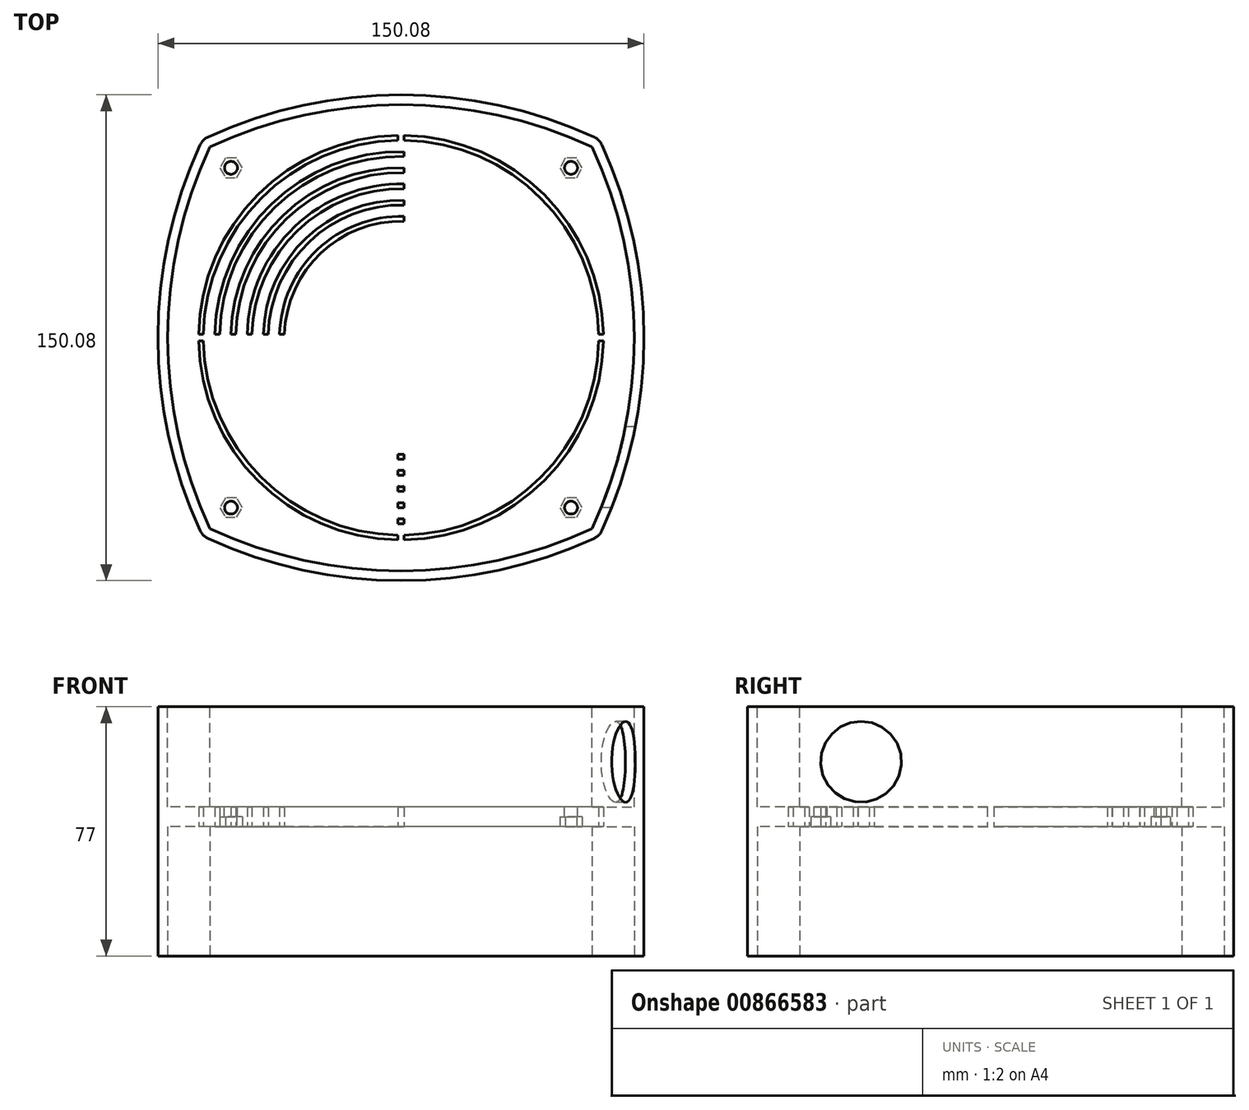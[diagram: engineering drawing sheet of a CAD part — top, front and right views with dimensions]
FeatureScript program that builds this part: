
annotation { "Feature Type Name" : "Feature", "Feature Type Description" : "" }
export const myFeature = defineFeature(function(context is Context, id is Id, definition is map)
    precondition{}
    {
        {
            var Q0;
            Q0=qCreatedBy(makeId("Top.planeOp"),FACE);
            var sketch = newSketch(context, id + "F0", { "sketchPlane" : qUnion([Q0])});
            skLineSegment(sketch, "E0.bottom", {"start": v(196, 49) * mm, "end": v(-196, 49) * mm, "construction": true});
            skLineSegment(sketch, "E0.top", {"start": v(196, -49) * mm, "end": v(-196, -49) * mm, "construction": true});
            skLineSegment(sketch, "E0.left", {"start": v(196, 49) * mm, "end": v(196, -49) * mm, "construction": true});
            skLineSegment(sketch, "E0.right", {"start": v(-196, 49) * mm, "end": v(-196, -49) * mm, "construction": true});
            skPoint(sketch, "E0.middle", {"position": v(0, 0) * mm});
            skLineSegment(sketch, "E1.bottom", {"start": v(207, 59) * mm, "end": v(-207, 59) * mm, "construction": true});
            skLineSegment(sketch, "E1.top", {"start": v(207, -59) * mm, "end": v(-207, -59) * mm, "construction": true});
            skLineSegment(sketch, "E1.left", {"start": v(207, 59) * mm, "end": v(207, -59) * mm, "construction": true});
            skLineSegment(sketch, "E1.right", {"start": v(-207, 59) * mm, "end": v(-207, -59) * mm, "construction": true});
            skLineSegment(sketch, "E2", {"start": v(0, -59) * mm, "end": v(0, 59) * mm, "construction": true});
            skLineSegment(sketch, "E3", {"start": v(-207, 0) * mm, "end": v(207, 0) * mm, "construction": true});
            skCircle(sketch, "E4", {"center": v(0, 0) * mm, "radius": 47.86 * mm});
            skLineSegment(sketch, "E5.bottom", {"start": v(59, 59) * mm, "end": v(-59, 59) * mm, "construction": true});
            skLineSegment(sketch, "E5.top", {"start": v(59, -59) * mm, "end": v(-59, -59) * mm, "construction": true});
            skLineSegment(sketch, "E5.left", {"start": v(59, 59) * mm, "end": v(59, -59) * mm, "construction": true});
            skLineSegment(sketch, "E5.right", {"start": v(-59, 59) * mm, "end": v(-59, -59) * mm, "construction": true});
            skArc(sketch, "E6", {"start": v(59, 59) * mm, "mid": v(0, 72.04) * mm, "end": v(-59, 59) * mm});
            skArc(sketch, "E7", {"start": v(59, -59) * mm, "mid": v(72.04, 0) * mm, "end": v(59, 59) * mm});
            skArc(sketch, "E8", {"start": v(-59, -59) * mm, "mid": v(0, -72.04) * mm, "end": v(59, -59) * mm});
            skArc(sketch, "E9", {"start": v(-59, 59) * mm, "mid": v(-72.04, 0) * mm, "end": v(-59, -59) * mm});
            skArc(sketch, "E10.0", {"start": v(61.26, 61.26) * mm, "mid": v(0, 75.04) * mm, "end": v(-61.26, 61.26) * mm});
            skArc(sketch, "E10.1", {"start": v(61.26, -61.26) * mm, "mid": v(75.04, 0) * mm, "end": v(61.26, 61.26) * mm});
            skArc(sketch, "E10.2", {"start": v(-61.26, -61.26) * mm, "mid": v(0, -75.04) * mm, "end": v(61.26, -61.26) * mm});
            skArc(sketch, "E10.3", {"start": v(-61.26, 61.26) * mm, "mid": v(-75.04, 0) * mm, "end": v(-61.26, -61.26) * mm});
            skSolve(sketch);
        }
        {
            var Q0;
            {var subQ8=sQuery(id+"F0.wireOp",EDGE,"E6");Q0=makeQuery(id+"F0.imprint","IMPRINT",FACE,{"disambiguationData":[TD([[makeQuery(id+"F0.imprint","IMPRINT",EDGE,{"derivedFrom":subQ8}),-1.0]])]});}
            var Q1;
            {var subQ0=sQuery(id+"F0.wireOp",EDGE,"E10.1");var subQ1=sQuery(id+"F0.wireOp",EDGE,"2c3d49d2-39e6-4b7c-b00d-7af9e24e8e71.0");var subQ2=makeQuery(id+"F0.imprint","INTERSECT",VERTEX,{"disambiguationData":[OD(0.0)],"derivedFrom":[subQ1,subQ0]});Q1=makeQuery(id+"F0.imprint","IMPRINT",FACE,{"disambiguationData":[TD([[makeQuery(id+"F0.imprint","IMPRINT",EDGE,{"disambiguationData":[TD([[subQ2,-1.0]])],"derivedFrom":subQ1}),1.0]])]});}
            extrude(context, id + "F1", {"entities" : qUnion([Q0, Q1]), "endBound" : BoundingType.SYMMETRIC, "depth" : 160 * mm, "offsetDistance" : 25 * mm});
        }
        {
            var Q0;
            Q0=qCreatedBy(makeId("Right.planeOp"),FACE);
            var sketch = newSketch(context, id + "F2", { "sketchPlane" : qUnion([Q0])});
            skCircle(sketch, "E11", {"center": v(-294.04, 1407.06) * mm, "radius": 1379.34 * mm});
            skLineSegment(sketch, "E12", {"start": v(0, 0) * mm, "end": v(-237.77, 0) * mm, "construction": true});
            skCircle(sketch, "E13.MirrorC", {"center": v(-294.04, -1407.06) * mm, "radius": 1379.34 * mm});
            skSolve(sketch);
        }
        {
            var Q0;
            Q0=makeQuery(id+"F2.imprint","IMPRINT",FACE,{"disambiguationData":[TD([[makeQuery(id+"F2.imprint","IMPRINT",EDGE,{"derivedFrom":sQuery(id+"F2.wireOp",EDGE,"E11")}),1.0]])]});
            var Q1;
            Q1=makeQuery(id+"F2.imprint","IMPRINT",FACE,{"disambiguationData":[TD([[makeQuery(id+"F2.imprint","IMPRINT",EDGE,{"derivedFrom":sQuery(id+"F2.wireOp",EDGE,"E13.MirrorC")}),-1.0]])]});
            extrude(context, id + "F3", {"entities" : qUnion([Q0, Q1]), "operationType" : NewBodyOperationType.REMOVE, "endBound" : BoundingType.SYMMETRIC, "oppositeDirection" : true, "depth" : 780 * mm, "offsetDistance" : 25 * mm});
        }
        {
            var Q0;
            Q0=qCreatedBy(makeId("Top.planeOp"),FACE);
            cPlane(context, id + "F4", {"entities" : qUnion([Q0]), "cplaneType" : CPlaneType.OFFSET, "offset" : 40 * mm, "width" : 150 * mm, "height" : 150 * mm});
        }
        {
            var Q0;
            Q0=qCreatedBy(id+"F4.planeOp",FACE);
            var sketch = newSketch(context, id + "F5", { "sketchPlane" : qUnion([Q0])});
            skLineSegment(sketch, "E14.bottom", {"start": v(59, 59) * mm, "end": v(-59, 59) * mm, "construction": true});
            skLineSegment(sketch, "E14.top", {"start": v(59, -59) * mm, "end": v(-59, -59) * mm, "construction": true});
            skLineSegment(sketch, "E14.left", {"start": v(59, 59) * mm, "end": v(59, -59) * mm, "construction": true});
            skLineSegment(sketch, "E14.right", {"start": v(-59, 59) * mm, "end": v(-59, -59) * mm, "construction": true});
            skPoint(sketch, "E14.middle", {"position": v(0, 0) * mm});
            skArc(sketch, "E15", {"start": v(59, 59) * mm, "mid": v(0, 72.04) * mm, "end": v(-59, 59) * mm});
            skArc(sketch, "E16", {"start": v(59, -59) * mm, "mid": v(72.04, 0) * mm, "end": v(59, 59) * mm});
            skArc(sketch, "E17", {"start": v(-59, -59) * mm, "mid": v(0, -72.04) * mm, "end": v(59, -59) * mm});
            skArc(sketch, "E18", {"start": v(-59, 59) * mm, "mid": v(-72.04, 0) * mm, "end": v(-59, -59) * mm});
            skSolve(sketch);
        }
        {
            var Q0;
            Q0=qCreatedBy(makeId("Top.planeOp"),FACE);
            var sketch = newSketch(context, id + "F6", { "sketchPlane" : qUnion([Q0])});
            skLineSegment(sketch, "E19.bottom", {"start": v(59, 59) * mm, "end": v(-59, 59) * mm, "construction": true});
            skLineSegment(sketch, "E19.top", {"start": v(59, -59) * mm, "end": v(-59, -59) * mm, "construction": true});
            skLineSegment(sketch, "E19.left", {"start": v(59, 59) * mm, "end": v(59, -59) * mm, "construction": true});
            skLineSegment(sketch, "E19.right", {"start": v(-59, 59) * mm, "end": v(-59, -59) * mm, "construction": true});
            skPoint(sketch, "E19.middle", {"position": v(0, 0) * mm});
            skArc(sketch, "E20", {"start": v(59, 59) * mm, "mid": v(0, 72.04) * mm, "end": v(-59, 59) * mm});
            skArc(sketch, "E21", {"start": v(59, -59) * mm, "mid": v(72.04, 0) * mm, "end": v(59, 59) * mm});
            skArc(sketch, "E22", {"start": v(-59, -59) * mm, "mid": v(0, -72.04) * mm, "end": v(59, -59) * mm});
            skArc(sketch, "E23", {"start": v(-59, 59) * mm, "mid": v(-72.04, 0) * mm, "end": v(-59, -59) * mm});
            skArc(sketch, "E24.0", {"start": v(61.26, 61.26) * mm, "mid": v(0, 75.04) * mm, "end": v(-61.26, 61.26) * mm});
            skArc(sketch, "E24.1", {"start": v(61.26, -61.26) * mm, "mid": v(75.04, 0) * mm, "end": v(61.26, 61.26) * mm});
            skArc(sketch, "E24.2", {"start": v(-61.26, -61.26) * mm, "mid": v(0, -75.04) * mm, "end": v(61.26, -61.26) * mm});
            skArc(sketch, "E24.3", {"start": v(-61.26, 61.26) * mm, "mid": v(-75.04, 0) * mm, "end": v(-61.26, -61.26) * mm});
            skSolve(sketch);
        }
        {
            var Q0;
            Q0=qSketchRegion(id+"F6",true);
            var Q1;
            Q1=makeQuery(id+"F0.imprint","IMPRINT",FACE,{"disambiguationData":[TD([[makeQuery(id+"F0.imprint","IMPRINT",EDGE,{"derivedFrom":sQuery(id+"F0.wireOp",EDGE,"E4")}),-1.0]])]});
            var Q2;
            Q2=makeQuery(id+"F6.imprint","IMPRINT",FACE,{"disambiguationData":[TD([[makeQuery(id+"F6.imprint","IMPRINT",EDGE,{"derivedFrom":sQuery(id+"F6.wireOp",EDGE,"E20")}),1.0]])]});
            extrude(context, id + "F7", {"entities" : qUnion([Q0, Q1, Q2]), "operationType" : NewBodyOperationType.ADD, "endBound" : BoundingType.SYMMETRIC, "depth" : 80 * mm, "offsetDistance" : 25 * mm});
        }
        {
            var Q0;
            Q0=qCreatedBy(makeId("Top.planeOp"),FACE);
            var sketch = newSketch(context, id + "F8", { "sketchPlane" : qUnion([Q0])});
            skCircle(sketch, "E25", {"center": v(0, 0) * mm, "radius": 47.86 * mm});
            skSolve(sketch);
        }
        {
            var Q1;
            Q1=qSketchRegion(id+"F5",true);
            var Q2;
            Q2=qSketchRegion(id+"F8",true);
            loft(context, id + "F9", {"operationType" : NewBodyOperationType.REMOVE, "sheetProfilesArray" : [{ "sheetProfileEntities" : qUnion([Q1]) }, { "sheetProfileEntities" : qUnion([Q2]) }]});
        }
        {
            var Q0;
            Q0=makeQuery(id+"F0.imprint","IMPRINT",FACE,{"disambiguationData":[TD([[makeQuery(id+"F0.imprint","IMPRINT",EDGE,{"derivedFrom":sQuery(id+"F0.wireOp",EDGE,"E4")}),1.0]])]});
            var sketch = newSketch(context, id + "F10", { "sketchPlane" : qUnion([Q0])});
            skCircle(sketch, "E26", {"center": v(0, 0) * mm, "radius": 42.86 * mm});
            skSolve(sketch);
        }
        {
            var Q0;
            Q0=makeQuery(id+"F10.imprint","IMPRINT",FACE,{"disambiguationData":[TD([[makeQuery(id+"F10.imprint","IMPRINT",EDGE,{"derivedFrom":sQuery(id+"F10.wireOp",EDGE,"E26")}),1.0]])]});
            extrude(context, id + "F11", {"entities" : qUnion([Q0]), "operationType" : NewBodyOperationType.REMOVE, "oppositeDirection" : true, "depth" : 3 * mm, "offsetDistance" : 25 * mm});
        }
        {
            var Q0;
            Q0=qCreatedBy(makeId("Top.planeOp"),FACE);
            cPlane(context, id + "F12", {"entities" : qUnion([Q0]), "cplaneType" : CPlaneType.OFFSET, "offset" : 3 * mm, "oppositeDirection" : true, "width" : 150 * mm, "height" : 150 * mm});
        }
        {
            var Q0;
            Q0=qCreatedBy(id+"F12.planeOp",FACE);
            var sketch = newSketch(context, id + "F13", { "sketchPlane" : qUnion([Q0])});
            skLineSegment(sketch, "E27.bottom", {"start": v(59, 59) * mm, "end": v(-59, 59) * mm, "construction": true});
            skLineSegment(sketch, "E27.top", {"start": v(59, -59) * mm, "end": v(-59, -59) * mm, "construction": true});
            skLineSegment(sketch, "E27.left", {"start": v(59, 59) * mm, "end": v(59, -59) * mm, "construction": true});
            skLineSegment(sketch, "E27.right", {"start": v(-59, 59) * mm, "end": v(-59, -59) * mm, "construction": true});
            skPoint(sketch, "E27.middle", {"position": v(0, 0) * mm});
            skArc(sketch, "E28", {"start": v(59, 59) * mm, "mid": v(0, 72.04) * mm, "end": v(-59, 59) * mm});
            skArc(sketch, "E29", {"start": v(59, -59) * mm, "mid": v(72.04, 0) * mm, "end": v(59, 59) * mm});
            skArc(sketch, "E30", {"start": v(-59, -59) * mm, "mid": v(0, -72.04) * mm, "end": v(59, -59) * mm});
            skArc(sketch, "E31", {"start": v(-59, 59) * mm, "mid": v(-72.04, 0) * mm, "end": v(-59, -59) * mm});
            skSolve(sketch);
        }
        {
            var Q0;
            Q0=qSketchRegion(id+"F13",true);
            extrude(context, id + "F14", {"entities" : qUnion([Q0]), "operationType" : NewBodyOperationType.REMOVE, "oppositeDirection" : true, "depth" : 31 * mm, "offsetDistance" : 25 * mm});
        }
        {
            var Q0;
            Q0=makeQuery(id+"F7.boolean.opBoolean","MERGE",FACE,{"derivedFrom":[makeQuery(id+"F7.opExtrude","CAP_FACE",FACE,{"disambiguationData":[OSD([sQuery(id+"F0.wireOp",EDGE,"E4"),sQuery(id+"F0.wireOp",EDGE,"E6"),sQuery(id+"F0.wireOp",EDGE,"E7"),sQuery(id+"F0.wireOp",EDGE,"E8"),sQuery(id+"F0.wireOp",EDGE,"E9")])],"isStart":true}),makeQuery(id+"F7.opExtrude","CAP_FACE",FACE,{"disambiguationData":[OSD([sQuery(id+"F6.wireOp",EDGE,"E24.0"),sQuery(id+"F6.wireOp",EDGE,"E24.1"),sQuery(id+"F6.wireOp",EDGE,"E24.2"),sQuery(id+"F6.wireOp",EDGE,"E24.3")])],"isStart":true})]});
            var sketch = newSketch(context, id + "F15", { "sketchPlane" : qUnion([Q0])});
            skCircle(sketch, "E32", {"center": v(0, 0) * mm, "radius": 62.5 * mm});
            skCircle(sketch, "E33", {"center": v(0, 0) * mm, "radius": 61 * mm});
            skCircle(sketch, "E34", {"center": v(0, 0) * mm, "radius": 57.5 * mm});
            skCircle(sketch, "E35", {"center": v(0, 0) * mm, "radius": 56 * mm});
            skCircle(sketch, "E36", {"center": v(0, 0) * mm, "radius": 52.5 * mm});
            skCircle(sketch, "E37", {"center": v(0, 0) * mm, "radius": 51 * mm});
            skCircle(sketch, "E38", {"center": v(0, 0) * mm, "radius": 47.5 * mm});
            skCircle(sketch, "E39", {"center": v(0, 0) * mm, "radius": 46 * mm});
            skCircle(sketch, "E40", {"center": v(0, 0) * mm, "radius": 42.5 * mm});
            skCircle(sketch, "E41", {"center": v(0, 0) * mm, "radius": 41 * mm});
            skCircle(sketch, "E42", {"center": v(0, 0) * mm, "radius": 37.5 * mm});
            skCircle(sketch, "E43", {"center": v(0, 0) * mm, "radius": 36 * mm});
            skLineSegment(sketch, "E44.bottom", {"start": v(1, -67) * mm, "end": v(-1, -67) * mm});
            skLineSegment(sketch, "E44.top", {"start": v(1, 67) * mm, "end": v(-1, 67) * mm});
            skLineSegment(sketch, "E44.left", {"start": v(1, -67) * mm, "end": v(1, 67) * mm});
            skLineSegment(sketch, "E44.right", {"start": v(-1, -67) * mm, "end": v(-1, 67) * mm});
            skLineSegment(sketch, "E45.bottom", {"start": v(67.5, -1) * mm, "end": v(-67.5, -1) * mm});
            skLineSegment(sketch, "E45.top", {"start": v(67.5, 1) * mm, "end": v(-67.5, 1) * mm});
            skLineSegment(sketch, "E45.left", {"start": v(67.5, -1) * mm, "end": v(67.5, 1) * mm});
            skLineSegment(sketch, "E45.right", {"start": v(-67.5, -1) * mm, "end": v(-67.5, 1) * mm});
            skSolve(sketch);
        }
        {
            var Q0;
            {var subQ0=sQuery(id+"F15.wireOp",EDGE,"E44.right");var subQ1=sQuery(id+"F15.wireOp",EDGE,"E32");var subQ2=makeQuery(id+"F15.imprint","INTERSECT",VERTEX,{"disambiguationData":[OD(0.0)],"derivedFrom":[subQ1,subQ0]});Q0=makeQuery(id+"F15.imprint","IMPRINT",FACE,{"disambiguationData":[TD([[makeQuery(id+"F15.imprint","IMPRINT",EDGE,{"disambiguationData":[TD([[subQ2,-1.0]])],"derivedFrom":subQ1}),1.0]])]});}
            var Q1;
            {var subQ0=sQuery(id+"F15.wireOp",EDGE,"E44.right");var subQ1=sQuery(id+"F15.wireOp",EDGE,"E34");var subQ2=makeQuery(id+"F15.imprint","INTERSECT",VERTEX,{"disambiguationData":[OD(0.0)],"derivedFrom":[subQ1,subQ0]});Q1=makeQuery(id+"F15.imprint","IMPRINT",FACE,{"disambiguationData":[TD([[makeQuery(id+"F15.imprint","IMPRINT",EDGE,{"disambiguationData":[TD([[subQ2,-1.0]])],"derivedFrom":subQ1}),1.0]])]});}
            var Q2;
            {var subQ0=sQuery(id+"F15.wireOp",EDGE,"E44.right");var subQ1=sQuery(id+"F15.wireOp",EDGE,"E36");var subQ2=makeQuery(id+"F15.imprint","INTERSECT",VERTEX,{"disambiguationData":[OD(0.0)],"derivedFrom":[subQ1,subQ0]});Q2=makeQuery(id+"F15.imprint","IMPRINT",FACE,{"disambiguationData":[TD([[makeQuery(id+"F15.imprint","IMPRINT",EDGE,{"disambiguationData":[TD([[subQ2,-1.0]])],"derivedFrom":subQ1}),1.0]])]});}
            var Q3;
            {var subQ0=sQuery(id+"F15.wireOp",EDGE,"E44.right");var subQ1=sQuery(id+"F15.wireOp",EDGE,"E38");var subQ2=makeQuery(id+"F15.imprint","INTERSECT",VERTEX,{"disambiguationData":[OD(0.0)],"derivedFrom":[subQ1,subQ0]});Q3=makeQuery(id+"F15.imprint","IMPRINT",FACE,{"disambiguationData":[TD([[makeQuery(id+"F15.imprint","IMPRINT",EDGE,{"disambiguationData":[TD([[subQ2,-1.0]])],"derivedFrom":subQ1}),1.0]])]});}
            var Q4;
            {var subQ0=sQuery(id+"F15.wireOp",EDGE,"E44.right");var subQ1=sQuery(id+"F15.wireOp",EDGE,"E40");var subQ2=makeQuery(id+"F15.imprint","INTERSECT",VERTEX,{"disambiguationData":[OD(0.0)],"derivedFrom":[subQ1,subQ0]});Q4=makeQuery(id+"F15.imprint","IMPRINT",FACE,{"disambiguationData":[TD([[makeQuery(id+"F15.imprint","IMPRINT",EDGE,{"disambiguationData":[TD([[subQ2,-1.0]])],"derivedFrom":subQ1}),1.0]])]});}
            var Q5;
            {var subQ0=sQuery(id+"F15.wireOp",EDGE,"E44.right");var subQ1=sQuery(id+"F15.wireOp",EDGE,"E42");var subQ2=makeQuery(id+"F15.imprint","INTERSECT",VERTEX,{"disambiguationData":[OD(0.0)],"derivedFrom":[subQ1,subQ0]});Q5=makeQuery(id+"F15.imprint","IMPRINT",FACE,{"disambiguationData":[TD([[makeQuery(id+"F15.imprint","IMPRINT",EDGE,{"disambiguationData":[TD([[subQ2,-1.0]])],"derivedFrom":subQ1}),1.0]])]});}
            var Q6;
            {var subQ0=sQuery(id+"F15.wireOp",EDGE,"E44.left");var subQ1=sQuery(id+"F15.wireOp",EDGE,"E42");var subQ2=makeQuery(id+"F15.imprint","INTERSECT",VERTEX,{"disambiguationData":[OD(0.0)],"derivedFrom":[subQ1,subQ0]});Q6=makeQuery(id+"F15.imprint","IMPRINT",FACE,{"disambiguationData":[TD([[makeQuery(id+"F15.imprint","IMPRINT",EDGE,{"disambiguationData":[TD([[subQ2,1.0]])],"derivedFrom":subQ1}),1.0]])]});}
            var Q7;
            {var subQ0=sQuery(id+"F15.wireOp",EDGE,"E44.left");var subQ1=sQuery(id+"F15.wireOp",EDGE,"E40");var subQ2=makeQuery(id+"F15.imprint","INTERSECT",VERTEX,{"disambiguationData":[OD(0.0)],"derivedFrom":[subQ1,subQ0]});Q7=makeQuery(id+"F15.imprint","IMPRINT",FACE,{"disambiguationData":[TD([[makeQuery(id+"F15.imprint","IMPRINT",EDGE,{"disambiguationData":[TD([[subQ2,1.0]])],"derivedFrom":subQ1}),1.0]])]});}
            var Q8;
            {var subQ0=sQuery(id+"F15.wireOp",EDGE,"E44.left");var subQ1=sQuery(id+"F15.wireOp",EDGE,"E38");var subQ2=makeQuery(id+"F15.imprint","INTERSECT",VERTEX,{"disambiguationData":[OD(0.0)],"derivedFrom":[subQ1,subQ0]});Q8=makeQuery(id+"F15.imprint","IMPRINT",FACE,{"disambiguationData":[TD([[makeQuery(id+"F15.imprint","IMPRINT",EDGE,{"disambiguationData":[TD([[subQ2,1.0]])],"derivedFrom":subQ1}),1.0]])]});}
            var Q9;
            {var subQ0=sQuery(id+"F15.wireOp",EDGE,"E44.left");var subQ1=sQuery(id+"F15.wireOp",EDGE,"E36");var subQ2=makeQuery(id+"F15.imprint","INTERSECT",VERTEX,{"disambiguationData":[OD(0.0)],"derivedFrom":[subQ1,subQ0]});Q9=makeQuery(id+"F15.imprint","IMPRINT",FACE,{"disambiguationData":[TD([[makeQuery(id+"F15.imprint","IMPRINT",EDGE,{"disambiguationData":[TD([[subQ2,1.0]])],"derivedFrom":subQ1}),1.0]])]});}
            var Q10;
            {var subQ0=sQuery(id+"F15.wireOp",EDGE,"E44.left");var subQ1=sQuery(id+"F15.wireOp",EDGE,"E34");var subQ2=makeQuery(id+"F15.imprint","INTERSECT",VERTEX,{"disambiguationData":[OD(0.0)],"derivedFrom":[subQ1,subQ0]});Q10=makeQuery(id+"F15.imprint","IMPRINT",FACE,{"disambiguationData":[TD([[makeQuery(id+"F15.imprint","IMPRINT",EDGE,{"disambiguationData":[TD([[subQ2,1.0]])],"derivedFrom":subQ1}),1.0]])]});}
            var Q11;
            {var subQ0=sQuery(id+"F15.wireOp",EDGE,"E44.left");var subQ1=sQuery(id+"F15.wireOp",EDGE,"E32");var subQ2=makeQuery(id+"F15.imprint","INTERSECT",VERTEX,{"disambiguationData":[OD(0.0)],"derivedFrom":[subQ1,subQ0]});Q11=makeQuery(id+"F15.imprint","IMPRINT",FACE,{"disambiguationData":[TD([[makeQuery(id+"F15.imprint","IMPRINT",EDGE,{"disambiguationData":[TD([[subQ2,1.0]])],"derivedFrom":subQ1}),1.0]])]});}
            var Q12;
            {var subQ0=sQuery(id+"F15.wireOp",EDGE,"E44.left");var subQ1=sQuery(id+"F15.wireOp",EDGE,"E42");var subQ2=makeQuery(id+"F15.imprint","INTERSECT",VERTEX,{"disambiguationData":[OD(1.0)],"derivedFrom":[subQ1,subQ0]});Q12=makeQuery(id+"F15.imprint","IMPRINT",FACE,{"disambiguationData":[TD([[makeQuery(id+"F15.imprint","IMPRINT",EDGE,{"disambiguationData":[TD([[subQ2,-1.0]])],"derivedFrom":subQ1}),1.0]])]});}
            var Q13;
            {var subQ0=sQuery(id+"F15.wireOp",EDGE,"E45.bottom");var subQ1=sQuery(id+"F15.wireOp",EDGE,"E42");var subQ2=makeQuery(id+"F15.imprint","INTERSECT",VERTEX,{"disambiguationData":[OD(0.0)],"derivedFrom":[subQ1,subQ0]});Q13=makeQuery(id+"F15.imprint","IMPRINT",FACE,{"disambiguationData":[TD([[makeQuery(id+"F15.imprint","IMPRINT",EDGE,{"disambiguationData":[TD([[subQ2,-1.0]])],"derivedFrom":subQ1}),1.0]])]});}
            var Q14;
            {var subQ0=sQuery(id+"F15.wireOp",EDGE,"E45.bottom");var subQ1=sQuery(id+"F15.wireOp",EDGE,"E40");var subQ2=makeQuery(id+"F15.imprint","INTERSECT",VERTEX,{"disambiguationData":[OD(0.0)],"derivedFrom":[subQ1,subQ0]});Q14=makeQuery(id+"F15.imprint","IMPRINT",FACE,{"disambiguationData":[TD([[makeQuery(id+"F15.imprint","IMPRINT",EDGE,{"disambiguationData":[TD([[subQ2,-1.0]])],"derivedFrom":subQ1}),1.0]])]});}
            var Q15;
            {var subQ0=sQuery(id+"F15.wireOp",EDGE,"E44.left");var subQ1=sQuery(id+"F15.wireOp",EDGE,"E40");var subQ2=makeQuery(id+"F15.imprint","INTERSECT",VERTEX,{"disambiguationData":[OD(1.0)],"derivedFrom":[subQ1,subQ0]});Q15=makeQuery(id+"F15.imprint","IMPRINT",FACE,{"disambiguationData":[TD([[makeQuery(id+"F15.imprint","IMPRINT",EDGE,{"disambiguationData":[TD([[subQ2,-1.0]])],"derivedFrom":subQ1}),1.0]])]});}
            var Q16;
            {var subQ0=sQuery(id+"F15.wireOp",EDGE,"E44.left");var subQ1=sQuery(id+"F15.wireOp",EDGE,"E38");var subQ2=makeQuery(id+"F15.imprint","INTERSECT",VERTEX,{"disambiguationData":[OD(1.0)],"derivedFrom":[subQ1,subQ0]});Q16=makeQuery(id+"F15.imprint","IMPRINT",FACE,{"disambiguationData":[TD([[makeQuery(id+"F15.imprint","IMPRINT",EDGE,{"disambiguationData":[TD([[subQ2,-1.0]])],"derivedFrom":subQ1}),1.0]])]});}
            var Q17;
            {var subQ0=sQuery(id+"F15.wireOp",EDGE,"E45.bottom");var subQ1=sQuery(id+"F15.wireOp",EDGE,"E38");var subQ2=makeQuery(id+"F15.imprint","INTERSECT",VERTEX,{"disambiguationData":[OD(0.0)],"derivedFrom":[subQ1,subQ0]});Q17=makeQuery(id+"F15.imprint","IMPRINT",FACE,{"disambiguationData":[TD([[makeQuery(id+"F15.imprint","IMPRINT",EDGE,{"disambiguationData":[TD([[subQ2,-1.0]])],"derivedFrom":subQ1}),1.0]])]});}
            var Q18;
            {var subQ0=sQuery(id+"F15.wireOp",EDGE,"E45.bottom");var subQ1=sQuery(id+"F15.wireOp",EDGE,"E36");var subQ2=makeQuery(id+"F15.imprint","INTERSECT",VERTEX,{"disambiguationData":[OD(0.0)],"derivedFrom":[subQ1,subQ0]});Q18=makeQuery(id+"F15.imprint","IMPRINT",FACE,{"disambiguationData":[TD([[makeQuery(id+"F15.imprint","IMPRINT",EDGE,{"disambiguationData":[TD([[subQ2,-1.0]])],"derivedFrom":subQ1}),1.0]])]});}
            var Q19;
            {var subQ0=sQuery(id+"F15.wireOp",EDGE,"E44.left");var subQ1=sQuery(id+"F15.wireOp",EDGE,"E36");var subQ2=makeQuery(id+"F15.imprint","INTERSECT",VERTEX,{"disambiguationData":[OD(1.0)],"derivedFrom":[subQ1,subQ0]});Q19=makeQuery(id+"F15.imprint","IMPRINT",FACE,{"disambiguationData":[TD([[makeQuery(id+"F15.imprint","IMPRINT",EDGE,{"disambiguationData":[TD([[subQ2,-1.0]])],"derivedFrom":subQ1}),1.0]])]});}
            var Q20;
            {var subQ0=sQuery(id+"F15.wireOp",EDGE,"E44.left");var subQ1=sQuery(id+"F15.wireOp",EDGE,"E34");var subQ2=makeQuery(id+"F15.imprint","INTERSECT",VERTEX,{"disambiguationData":[OD(1.0)],"derivedFrom":[subQ1,subQ0]});Q20=makeQuery(id+"F15.imprint","IMPRINT",FACE,{"disambiguationData":[TD([[makeQuery(id+"F15.imprint","IMPRINT",EDGE,{"disambiguationData":[TD([[subQ2,-1.0]])],"derivedFrom":subQ1}),1.0]])]});}
            var Q21;
            {var subQ0=sQuery(id+"F15.wireOp",EDGE,"E45.bottom");var subQ1=sQuery(id+"F15.wireOp",EDGE,"E34");var subQ2=makeQuery(id+"F15.imprint","INTERSECT",VERTEX,{"disambiguationData":[OD(0.0)],"derivedFrom":[subQ1,subQ0]});Q21=makeQuery(id+"F15.imprint","IMPRINT",FACE,{"disambiguationData":[TD([[makeQuery(id+"F15.imprint","IMPRINT",EDGE,{"disambiguationData":[TD([[subQ2,-1.0]])],"derivedFrom":subQ1}),1.0]])]});}
            var Q22;
            {var subQ0=sQuery(id+"F15.wireOp",EDGE,"E45.bottom");var subQ1=sQuery(id+"F15.wireOp",EDGE,"E32");var subQ2=makeQuery(id+"F15.imprint","INTERSECT",VERTEX,{"disambiguationData":[OD(0.0)],"derivedFrom":[subQ1,subQ0]});Q22=makeQuery(id+"F15.imprint","IMPRINT",FACE,{"disambiguationData":[TD([[makeQuery(id+"F15.imprint","IMPRINT",EDGE,{"disambiguationData":[TD([[subQ2,-1.0]])],"derivedFrom":subQ1}),1.0]])]});}
            var Q23;
            {var subQ0=sQuery(id+"F15.wireOp",EDGE,"E44.left");var subQ1=sQuery(id+"F15.wireOp",EDGE,"E32");var subQ2=makeQuery(id+"F15.imprint","INTERSECT",VERTEX,{"disambiguationData":[OD(1.0)],"derivedFrom":[subQ1,subQ0]});Q23=makeQuery(id+"F15.imprint","IMPRINT",FACE,{"disambiguationData":[TD([[makeQuery(id+"F15.imprint","IMPRINT",EDGE,{"disambiguationData":[TD([[subQ2,-1.0]])],"derivedFrom":subQ1}),1.0]])]});}
            extrude(context, id + "F16", {"entities" : qUnion([Q0, Q1, Q2, Q3, Q4, Q5, Q6, Q7, Q8, Q9, Q10, Q11, Q12, Q13, Q14, Q15, Q16, Q17, Q18, Q19, Q20, Q21, Q22, Q23]), "operationType" : NewBodyOperationType.REMOVE, "oppositeDirection" : true, "depth" : 25 * mm, "offsetDistance" : 25 * mm});
        }
        {
            var Q0;
            Q0=makeQuery(id+"F1.opExtrude","SWEPT_EDGE",EDGE,{"disambiguationData":[OSD([sQuery(id+"F0.wireOp",EDGE,"E10.0"),sQuery(id+"F0.wireOp",EDGE,"E10.3")])]});
            var Q1;
            Q1=makeQuery(id+"F1.opExtrude","SWEPT_EDGE",EDGE,{"disambiguationData":[OSD([sQuery(id+"F0.wireOp",EDGE,"E10.2"),sQuery(id+"F0.wireOp",EDGE,"E10.3")])]});
            var Q2;
            Q2=makeQuery(id+"F1.opExtrude","SWEPT_EDGE",EDGE,{"disambiguationData":[OSD([sQuery(id+"F0.wireOp",EDGE,"E10.0"),sQuery(id+"F0.wireOp",EDGE,"E10.1")])]});
            var Q3;
            Q3=makeQuery(id+"F1.opExtrude","SWEPT_EDGE",EDGE,{"disambiguationData":[OSD([sQuery(id+"F0.wireOp",EDGE,"E10.1"),sQuery(id+"F0.wireOp",EDGE,"E10.2")])]});
            var Q4;
            {var subQ0=sQuery(id+"F0.wireOp",EDGE,"E9");var subQ1=sQuery(id+"F0.wireOp",EDGE,"E6");Q4=makeQuery(id+"F7.boolean.opBoolean","SPLIT",EDGE,{"disambiguationData":[TD([makeQuery(id+"F3.boolean.opBoolean","COPY",FACE,{"derivedFrom":makeQuery(id+"F3.opExtrude","SWEPT_FACE",FACE,{"disambiguationData":[OSD([sQuery(id+"F2.wireOp",EDGE,"E11")])]})})])],"derivedFrom":makeQuery(id+"F1.opExtrude","SWEPT_EDGE",EDGE,{"disambiguationData":[OSD([subQ1,subQ0])]})});}
            var Q5;
            {var subQ0=sQuery(id+"F0.wireOp",EDGE,"E7");var subQ1=sQuery(id+"F0.wireOp",EDGE,"E6");Q5=makeQuery(id+"F7.boolean.opBoolean","SPLIT",EDGE,{"disambiguationData":[TD([makeQuery(id+"F3.boolean.opBoolean","COPY",FACE,{"derivedFrom":makeQuery(id+"F3.opExtrude","SWEPT_FACE",FACE,{"disambiguationData":[OSD([sQuery(id+"F2.wireOp",EDGE,"E11")])]})})])],"derivedFrom":makeQuery(id+"F1.opExtrude","SWEPT_EDGE",EDGE,{"disambiguationData":[OSD([subQ1,subQ0])]})});}
            var Q6;
            {var subQ0=sQuery(id+"F0.wireOp",EDGE,"E9");var subQ1=sQuery(id+"F0.wireOp",EDGE,"E8");Q6=makeQuery(id+"F7.boolean.opBoolean","SPLIT",EDGE,{"disambiguationData":[TD([makeQuery(id+"F3.boolean.opBoolean","COPY",FACE,{"derivedFrom":makeQuery(id+"F3.opExtrude","SWEPT_FACE",FACE,{"disambiguationData":[OSD([sQuery(id+"F2.wireOp",EDGE,"E11")])]})})])],"derivedFrom":makeQuery(id+"F1.opExtrude","SWEPT_EDGE",EDGE,{"disambiguationData":[OSD([subQ1,subQ0])]})});}
            var Q7;
            {var subQ0=sQuery(id+"F0.wireOp",EDGE,"E8");var subQ1=sQuery(id+"F0.wireOp",EDGE,"E7");Q7=makeQuery(id+"F7.boolean.opBoolean","SPLIT",EDGE,{"disambiguationData":[TD([makeQuery(id+"F3.boolean.opBoolean","COPY",FACE,{"derivedFrom":makeQuery(id+"F3.opExtrude","SWEPT_FACE",FACE,{"disambiguationData":[OSD([sQuery(id+"F2.wireOp",EDGE,"E11")])]})})])],"derivedFrom":makeQuery(id+"F1.opExtrude","SWEPT_EDGE",EDGE,{"disambiguationData":[OSD([subQ1,subQ0])]})});}
            var Q8;
            {var subQ0=sQuery(id+"F0.wireOp",EDGE,"E8");var subQ1=sQuery(id+"F0.wireOp",EDGE,"E7");Q8=makeQuery(id+"F7.boolean.opBoolean","SPLIT",EDGE,{"disambiguationData":[TD([makeQuery(id+"F3.boolean.opBoolean","COPY",FACE,{"derivedFrom":makeQuery(id+"F3.opExtrude","SWEPT_FACE",FACE,{"disambiguationData":[OSD([sQuery(id+"F2.wireOp",EDGE,"E13.MirrorC")])]})})])],"derivedFrom":makeQuery(id+"F1.opExtrude","SWEPT_EDGE",EDGE,{"disambiguationData":[OSD([subQ1,subQ0])]})});}
            var Q9;
            {var subQ0=sQuery(id+"F0.wireOp",EDGE,"E9");var subQ1=sQuery(id+"F0.wireOp",EDGE,"E8");Q9=makeQuery(id+"F7.boolean.opBoolean","SPLIT",EDGE,{"disambiguationData":[TD([makeQuery(id+"F3.boolean.opBoolean","COPY",FACE,{"derivedFrom":makeQuery(id+"F3.opExtrude","SWEPT_FACE",FACE,{"disambiguationData":[OSD([sQuery(id+"F2.wireOp",EDGE,"E13.MirrorC")])]})})])],"derivedFrom":makeQuery(id+"F1.opExtrude","SWEPT_EDGE",EDGE,{"disambiguationData":[OSD([subQ1,subQ0])]})});}
            var Q10;
            {var subQ0=sQuery(id+"F0.wireOp",EDGE,"E9");var subQ1=sQuery(id+"F0.wireOp",EDGE,"E6");Q10=makeQuery(id+"F7.boolean.opBoolean","SPLIT",EDGE,{"disambiguationData":[TD([makeQuery(id+"F3.boolean.opBoolean","COPY",FACE,{"derivedFrom":makeQuery(id+"F3.opExtrude","SWEPT_FACE",FACE,{"disambiguationData":[OSD([sQuery(id+"F2.wireOp",EDGE,"E13.MirrorC")])]})})])],"derivedFrom":makeQuery(id+"F1.opExtrude","SWEPT_EDGE",EDGE,{"disambiguationData":[OSD([subQ1,subQ0])]})});}
            var Q11;
            {var subQ0=sQuery(id+"F0.wireOp",EDGE,"E7");var subQ1=sQuery(id+"F0.wireOp",EDGE,"E6");Q11=makeQuery(id+"F7.boolean.opBoolean","SPLIT",EDGE,{"disambiguationData":[TD([makeQuery(id+"F3.boolean.opBoolean","COPY",FACE,{"derivedFrom":makeQuery(id+"F3.opExtrude","SWEPT_FACE",FACE,{"disambiguationData":[OSD([sQuery(id+"F2.wireOp",EDGE,"E13.MirrorC")])]})})])],"derivedFrom":makeQuery(id+"F1.opExtrude","SWEPT_EDGE",EDGE,{"disambiguationData":[OSD([subQ1,subQ0])]})});}
            fillet(context, id + "F17", {"entities" : qUnion([Q0, Q1, Q2, Q3, Q4, Q5, Q6, Q7, Q8, Q9, Q10, Q11]), "radius" : 5 * mm, "tangentPropagation" : true, "allowEdgeOverflow" : false});
        }
        {
            var Q0;
            Q0=qCreatedBy(makeId("Top.planeOp"),FACE);
            cPlane(context, id + "F18", {"entities" : qUnion([Q0]), "cplaneType" : CPlaneType.OFFSET, "offset" : 50 * mm, "width" : 150 * mm, "height" : 150 * mm});
        }
        {
            var Q0;
            Q0=qCreatedBy(id+"F18.planeOp",FACE);
            var sketch = newSketch(context, id + "F19", { "sketchPlane" : qUnion([Q0])});
            skLineSegment(sketch, "E46.bottom", {"start": v(52.5, 52.5) * mm, "end": v(-52.5, 52.5) * mm, "construction": true});
            skLineSegment(sketch, "E46.top", {"start": v(52.5, -52.5) * mm, "end": v(-52.5, -52.5) * mm, "construction": true});
            skLineSegment(sketch, "E46.left", {"start": v(52.5, 52.5) * mm, "end": v(52.5, -52.5) * mm, "construction": true});
            skLineSegment(sketch, "E46.right", {"start": v(-52.5, 52.5) * mm, "end": v(-52.5, -52.5) * mm, "construction": true});
            skPoint(sketch, "E46.middle", {"position": v(0, 0) * mm});
            skCircle(sketch, "E47", {"center": v(-52.5, 52.5) * mm, "radius": 2 * mm});
            skCircle(sketch, "E48", {"center": v(52.5, 52.5) * mm, "radius": 2 * mm});
            skCircle(sketch, "E49", {"center": v(52.5, -52.5) * mm, "radius": 2 * mm});
            skCircle(sketch, "E50", {"center": v(-52.5, -52.5) * mm, "radius": 2 * mm});
            skSolve(sketch);
        }
        {
            var Q0;
            Q0=sQuery(id+"F19.wireOp",VERTEX,"E46.bottom.end");
            var Q1;
            Q1=sQuery(id+"F19.wireOp",VERTEX,"E46.bottom.start");
            var Q2;
            Q2=sQuery(id+"F19.wireOp",VERTEX,"E46.top.start");
            var Q3;
            Q3=sQuery(id+"F19.wireOp",VERTEX,"E46.top.end");
            var Q4;
            Q4=makeQuery(id+"F1.opExtrude","SWEPT_BODY",BODY,{"disambiguationData":[OSD([sQuery(id+"F0.wireOp",EDGE,"E6"),sQuery(id+"F0.wireOp",EDGE,"E7"),sQuery(id+"F0.wireOp",EDGE,"E8"),sQuery(id+"F0.wireOp",EDGE,"E9"),sQuery(id+"F0.wireOp",EDGE,"E10.0"),sQuery(id+"F0.wireOp",EDGE,"E10.1"),sQuery(id+"F0.wireOp",EDGE,"E10.2"),sQuery(id+"F0.wireOp",EDGE,"E10.3")])]});
            hole(context, id + "F20", {"style" : HoleStyle.C_BORE, "endStyle" : HoleEndStyle.THROUGH, "holeDiameter" : 4 * mm, "cBoreDiameter" : 8 * mm, "cBoreDepth" : 5 * mm, "majorDiameter" : 5 * mm, "isTappedThrough" : true, "tappedDepth" : 12 * mm, "tapClearance" : 3, "locations" : qUnion([Q0, Q1, Q2, Q3]), "scope" : qUnion([Q4])});
        }
        {
            var Q0;
            Q0=makeQuery(id+"F7.boolean.opBoolean","MERGE",FACE,{"derivedFrom":[makeQuery(id+"F7.opExtrude","CAP_FACE",FACE,{"disambiguationData":[OSD([sQuery(id+"F0.wireOp",EDGE,"E4"),sQuery(id+"F0.wireOp",EDGE,"E6"),sQuery(id+"F0.wireOp",EDGE,"E7"),sQuery(id+"F0.wireOp",EDGE,"E8"),sQuery(id+"F0.wireOp",EDGE,"E9")])],"isStart":true}),makeQuery(id+"F7.opExtrude","CAP_FACE",FACE,{"disambiguationData":[OSD([sQuery(id+"F6.wireOp",EDGE,"E24.0"),sQuery(id+"F6.wireOp",EDGE,"E24.1"),sQuery(id+"F6.wireOp",EDGE,"E24.2"),sQuery(id+"F6.wireOp",EDGE,"E24.3")])],"isStart":true})]});
            var sketch = newSketch(context, id + "F21", { "sketchPlane" : qUnion([Q0])});
            skCircle(sketch, "E51.cCircle", {"center": v(-52.5, 52.5) * mm, "radius": 3 * mm, "construction": true});
            skLineSegment(sketch, "E51.0", {"start": v(-54.23, 55.5) * mm, "end": v(-50.77, 55.5) * mm});
            skLineSegment(sketch, "E51.1", {"start": v(-50.77, 55.5) * mm, "end": v(-49.04, 52.5) * mm});
            skLineSegment(sketch, "E51.2", {"start": v(-49.04, 52.5) * mm, "end": v(-50.77, 49.5) * mm});
            skLineSegment(sketch, "E51.3", {"start": v(-50.77, 49.5) * mm, "end": v(-54.23, 49.5) * mm});
            skLineSegment(sketch, "E51.4", {"start": v(-54.23, 49.5) * mm, "end": v(-55.96, 52.5) * mm});
            skLineSegment(sketch, "E51.5", {"start": v(-55.96, 52.5) * mm, "end": v(-54.23, 55.5) * mm});
            skPoint(sketch, "E51.0.midPoint", {"position": v(-52.5, 55.5) * mm});
            skCircle(sketch, "E52.cCircle", {"center": v(52.5, 52.5) * mm, "radius": 3 * mm, "construction": true});
            skLineSegment(sketch, "E52.0", {"start": v(50.77, 55.5) * mm, "end": v(54.23, 55.5) * mm});
            skLineSegment(sketch, "E52.1", {"start": v(54.23, 55.5) * mm, "end": v(55.96, 52.5) * mm});
            skLineSegment(sketch, "E52.2", {"start": v(55.96, 52.5) * mm, "end": v(54.23, 49.5) * mm});
            skLineSegment(sketch, "E52.3", {"start": v(54.23, 49.5) * mm, "end": v(50.77, 49.5) * mm});
            skLineSegment(sketch, "E52.4", {"start": v(50.77, 49.5) * mm, "end": v(49.04, 52.5) * mm});
            skLineSegment(sketch, "E52.5", {"start": v(49.04, 52.5) * mm, "end": v(50.77, 55.5) * mm});
            skPoint(sketch, "E52.0.midPoint", {"position": v(52.5, 55.5) * mm});
            skCircle(sketch, "E53.cCircle", {"center": v(52.5, -52.5) * mm, "radius": 3 * mm, "construction": true});
            skLineSegment(sketch, "E53.0", {"start": v(50.77, -49.5) * mm, "end": v(54.23, -49.5) * mm});
            skLineSegment(sketch, "E53.1", {"start": v(54.23, -49.5) * mm, "end": v(55.96, -52.5) * mm});
            skLineSegment(sketch, "E53.2", {"start": v(55.96, -52.5) * mm, "end": v(54.23, -55.5) * mm});
            skLineSegment(sketch, "E53.3", {"start": v(54.23, -55.5) * mm, "end": v(50.77, -55.5) * mm});
            skLineSegment(sketch, "E53.4", {"start": v(50.77, -55.5) * mm, "end": v(49.04, -52.5) * mm});
            skLineSegment(sketch, "E53.5", {"start": v(49.04, -52.5) * mm, "end": v(50.77, -49.5) * mm});
            skPoint(sketch, "E53.0.midPoint", {"position": v(52.5, -49.5) * mm});
            skCircle(sketch, "E54.cCircle", {"center": v(-52.5, -52.5) * mm, "radius": 3 * mm, "construction": true});
            skLineSegment(sketch, "E54.0", {"start": v(-54.23, -49.5) * mm, "end": v(-50.77, -49.5) * mm});
            skLineSegment(sketch, "E54.1", {"start": v(-50.77, -49.5) * mm, "end": v(-49.04, -52.5) * mm});
            skLineSegment(sketch, "E54.2", {"start": v(-49.04, -52.5) * mm, "end": v(-50.77, -55.5) * mm});
            skLineSegment(sketch, "E54.3", {"start": v(-50.77, -55.5) * mm, "end": v(-54.23, -55.5) * mm});
            skLineSegment(sketch, "E54.4", {"start": v(-54.23, -55.5) * mm, "end": v(-55.96, -52.5) * mm});
            skLineSegment(sketch, "E54.5", {"start": v(-55.96, -52.5) * mm, "end": v(-54.23, -49.5) * mm});
            skPoint(sketch, "E54.0.midPoint", {"position": v(-52.5, -49.5) * mm});
            skSolve(sketch);
        }
        {
            var Q0;
            Q0=makeQuery(id+"F21.imprint","IMPRINT",FACE,{"disambiguationData":[TD([[makeQuery(id+"F21.imprint","IMPRINT",EDGE,{"derivedFrom":sQuery(id+"F21.wireOp",EDGE,"E51.0")}),-1.0]])]});
            var Q1;
            Q1=makeQuery(id+"F21.imprint","IMPRINT",FACE,{"disambiguationData":[TD([[makeQuery(id+"F21.imprint","IMPRINT",EDGE,{"derivedFrom":sQuery(id+"F21.wireOp",EDGE,"E52.0")}),-1.0]])]});
            var Q2;
            Q2=makeQuery(id+"F21.imprint","IMPRINT",FACE,{"disambiguationData":[TD([[makeQuery(id+"F21.imprint","IMPRINT",EDGE,{"derivedFrom":sQuery(id+"F21.wireOp",EDGE,"E53.0")}),-1.0]])]});
            var Q3;
            Q3=makeQuery(id+"F21.imprint","IMPRINT",FACE,{"disambiguationData":[TD([[makeQuery(id+"F21.imprint","IMPRINT",EDGE,{"derivedFrom":sQuery(id+"F21.wireOp",EDGE,"E54.0")}),-1.0]])]});
            extrude(context, id + "F22", {"entities" : qUnion([Q0, Q1, Q2, Q3]), "operationType" : NewBodyOperationType.REMOVE, "oppositeDirection" : true, "depth" : 3 * mm, "offsetDistance" : 25 * mm});
        }
        {
            var Q0;
            Q0=qCreatedBy(makeId("Right.planeOp"),FACE);
            var sketch = newSketch(context, id + "F23", { "sketchPlane" : qUnion([Q0])});
            skCircle(sketch, "E55", {"center": v(-40, -20) * mm, "radius": 12.5 * mm});
            skSolve(sketch);
        }
        {
            var Q0;
            Q0=qSketchRegion(id+"F23",true);
            extrude(context, id + "F24", {"entities" : qUnion([Q0]), "operationType" : NewBodyOperationType.REMOVE, "depth" : 249 * mm, "offsetDistance" : 25 * mm});
        }
        {
            var Q0;
            Q0=qCreatedBy(id+"F12.planeOp",FACE);
            var sketch = newSketch(context, id + "F25", { "sketchPlane" : qUnion([Q0])});
            skCircle(sketch, "E56", {"center": v(0, 0) * mm, "radius": 125 * mm});
            skSolve(sketch);
        }
        {
            var Q0;
            Q0=makeQuery(id+"F25.imprint","IMPRINT",FACE,{"disambiguationData":[TD([[makeQuery(id+"F25.imprint","IMPRINT",EDGE,{"derivedFrom":sQuery(id+"F25.wireOp",EDGE,"E56")}),1.0]])]});
            extrude(context, id + "F26", {"entities" : qUnion([Q0]), "operationType" : NewBodyOperationType.REMOVE, "depth" : 94 * mm, "offsetDistance" : 25 * mm});
        }
    });
